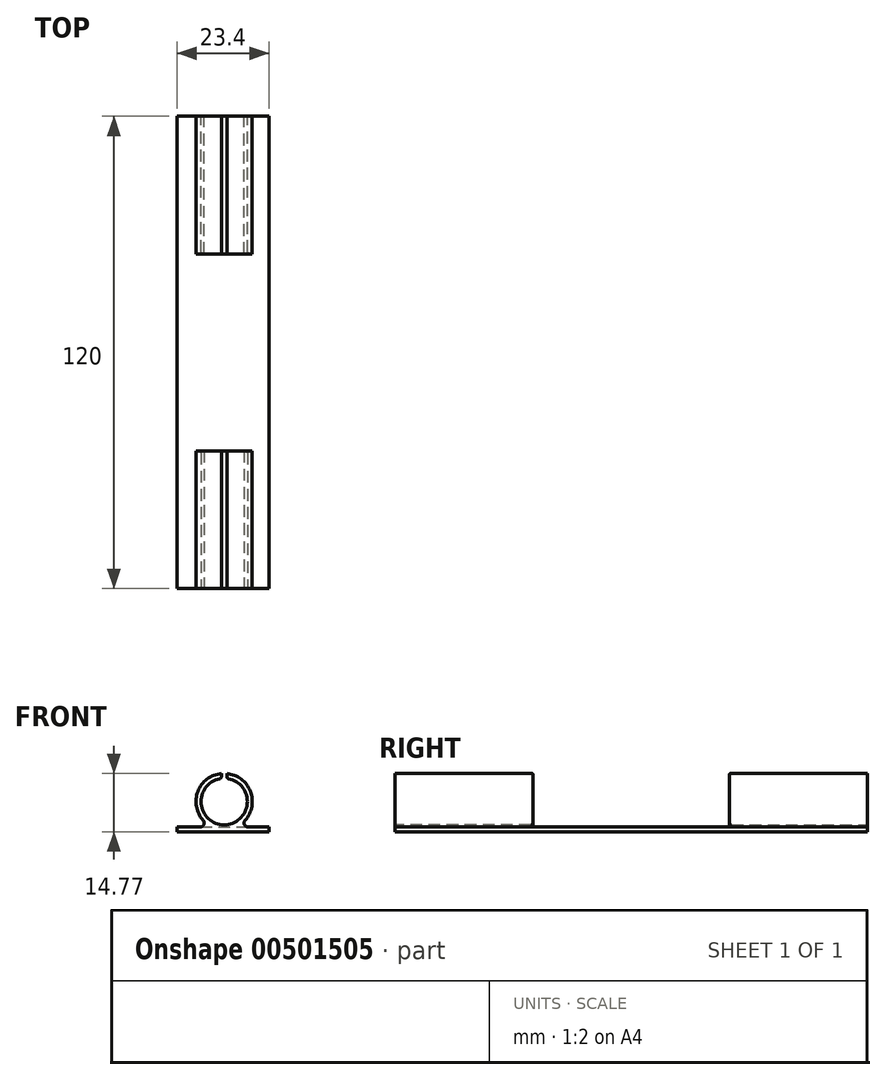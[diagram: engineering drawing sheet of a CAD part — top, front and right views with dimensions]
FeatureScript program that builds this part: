
annotation { "Feature Type Name" : "Feature", "Feature Type Description" : "" }
export const myFeature = defineFeature(function(context is Context, id is Id, definition is map)
    precondition{}
    {
        {
            var Q0;
            Q0=qCreatedBy(makeId("Top.planeOp"),FACE);
            var sketch = newSketch(context, id + "F0", { "sketchPlane" : qUnion([Q0])});
            skLineSegment(sketch, "E0.bottom", {"start": v(0, 0) * mm, "end": v(23.4, 0) * mm});
            skLineSegment(sketch, "E0.top", {"start": v(0, -60) * mm, "end": v(23.4, -60) * mm});
            skLineSegment(sketch, "E0.left", {"start": v(0, 0) * mm, "end": v(0, -60) * mm});
            skLineSegment(sketch, "E0.right", {"start": v(23.4, 0) * mm, "end": v(23.4, -60) * mm});
            skSolve(sketch);
        }
        {
            var Q0;
            Q0=makeQuery(id+"F0.imprint","IMPRINT",FACE,{"disambiguationData":[TD([[makeQuery(id+"F0.imprint","IMPRINT",EDGE,{"derivedFrom":sQuery(id+"F0.wireOp",EDGE,"E0.bottom")}),-1.0]])]});
            extrude(context, id + "F1", {"entities" : qUnion([Q0]), "depth" : 1.2 * mm});
        }
        {
            var Q0;
            Q0=qCreatedBy(makeId("Front.planeOp"),FACE);
            var sketch = newSketch(context, id + "F2", { "sketchPlane" : qUnion([Q0])});
            skCircle(sketch, "E1", {"center": v(12, 7.65) * mm, "radius": 5.9 * mm});
            skCircle(sketch, "E2", {"center": v(12, 7.65) * mm, "radius": 7.15 * mm});
            skLineSegment(sketch, "E3", {"start": v(0, 0.88) * mm, "end": v(0, 11.03) * mm, "construction": true});
            skLineSegment(sketch, "E4.bottom", {"start": v(12, 7.65) * mm, "end": v(12, 7.65) * mm});
            skLineSegment(sketch, "E5.bottom", {"start": v(12, 15.33) * mm, "end": v(11.3, 15.33) * mm});
            skLineSegment(sketch, "E5.top", {"start": v(12, 12.93) * mm, "end": v(11.3, 12.93) * mm});
            skLineSegment(sketch, "E5.left", {"start": v(12, 15.33) * mm, "end": v(12, 12.93) * mm});
            skLineSegment(sketch, "E5.right", {"start": v(11.3, 15.33) * mm, "end": v(11.3, 12.93) * mm});
            skLineSegment(sketch, "E6.MirrorCS", {"start": v(12, 15.33) * mm, "end": v(12.7, 15.33) * mm});
            skLineSegment(sketch, "E7.MirrorCS", {"start": v(12.7, 15.33) * mm, "end": v(12.7, 12.93) * mm});
            skLineSegment(sketch, "E8.MirrorCS", {"start": v(12, 12.93) * mm, "end": v(12.7, 12.93) * mm});
            skSolve(sketch);
        }
        {
            var Q0;
            {var subQ0=sQuery(id+"F2.wireOp",EDGE,"E7.MirrorCS");var subQ1=sQuery(id+"F2.wireOp",EDGE,"E1");var subQ2=makeQuery(id+"F2.imprint","INTERSECT",VERTEX,{"derivedFrom":[subQ1,subQ0]});Q0=makeQuery(id+"F2.imprint","IMPRINT",FACE,{"disambiguationData":[TD([[makeQuery(id+"F2.imprint","IMPRINT",EDGE,{"disambiguationData":[TD([[subQ2,1.0]])],"derivedFrom":subQ1}),-1.0]])]});}
            extrude(context, id + "F3", {"entities" : qUnion([Q0]), "operationType" : NewBodyOperationType.ADD, "depth" : 35 * mm});
        }
        {
            var Q0;
            Q0=makeQuery(id+"F3.boolean.opBoolean","INTERSECT",EDGE,{"disambiguationData":[OD(1.0)],"derivedFrom":[makeQuery(id+"F1.opExtrude","CAP_FACE",FACE,{"disambiguationData":[OSD([sQuery(id+"F0.wireOp",EDGE,"E0.bottom"),sQuery(id+"F0.wireOp",EDGE,"E0.top"),sQuery(id+"F0.wireOp",EDGE,"E0.left"),sQuery(id+"F0.wireOp",EDGE,"E0.right")])],"isStart":false}),makeQuery(id+"F3.opExtrude","SWEPT_FACE",FACE,{"disambiguationData":[OSD([sQuery(id+"F2.wireOp",EDGE,"E2")])]})]});
            fillet(context, id + "F4", {"entities" : qUnion([Q0]), "radius" : 1 * mm, "tangentPropagation" : true, "allowEdgeOverflow" : false});
        }
        {
            var Q0;
            Q0=makeQuery(id+"F3.boolean.opBoolean","INTERSECT",EDGE,{"disambiguationData":[OD(0.0)],"derivedFrom":[makeQuery(id+"F1.opExtrude","CAP_FACE",FACE,{"disambiguationData":[OSD([sQuery(id+"F0.wireOp",EDGE,"E0.bottom"),sQuery(id+"F0.wireOp",EDGE,"E0.top"),sQuery(id+"F0.wireOp",EDGE,"E0.left"),sQuery(id+"F0.wireOp",EDGE,"E0.right")])],"isStart":false}),makeQuery(id+"F3.opExtrude","SWEPT_FACE",FACE,{"disambiguationData":[OSD([sQuery(id+"F2.wireOp",EDGE,"E2")])]})]});
            fillet(context, id + "F5", {"entities" : qUnion([Q0]), "radius" : 1 * mm, "tangentPropagation" : true, "allowEdgeOverflow" : false});
        }
        {
            var Q0;
            Q0=makeQuery(id+"F3.opExtrude","CAP_EDGE",EDGE,{"disambiguationData":[OSD([sQuery(id+"F2.wireOp",EDGE,"E1")])],"isStart":false});
            fillet(context, id + "F6", {"entities" : qUnion([Q0]), "radius" : 0.5 * mm, "tangentPropagation" : true, "allowEdgeOverflow" : false});
        }
        {
            var Q0;
            Q0=makeQuery(id+"F3.opExtrude","SWEPT_EDGE",EDGE,{"disambiguationData":[OSD([sQuery(id+"F2.wireOp",EDGE,"E1"),sQuery(id+"F2.wireOp",EDGE,"E7.MirrorCS")])]});
            var Q1;
            Q1=makeQuery(id+"F3.opExtrude","SWEPT_EDGE",EDGE,{"disambiguationData":[OSD([sQuery(id+"F2.wireOp",EDGE,"E1"),sQuery(id+"F2.wireOp",EDGE,"E5.right")])]});
            fillet(context, id + "F7", {"entities" : qUnion([Q0, Q1]), "radius" : 0.5 * mm, "tangentPropagation" : true, "allowEdgeOverflow" : false});
        }
        {
            var Q0;
            Q0=makeQuery(id+"F1.opExtrude","SWEPT_BODY",BODY,{"disambiguationData":[OSD([sQuery(id+"F0.wireOp",EDGE,"E0.bottom"),sQuery(id+"F0.wireOp",EDGE,"E0.top"),sQuery(id+"F0.wireOp",EDGE,"E0.left"),sQuery(id+"F0.wireOp",EDGE,"E0.right")])]});
            var Q1;
            Q1=makeQuery(id+"F1.opExtrude","SWEPT_FACE",FACE,{"disambiguationData":[OSD([sQuery(id+"F0.wireOp",EDGE,"E0.top")])]});
            mirror(context, id + "F8", {"operationType" : NewBodyOperationType.ADD, "entities" : qUnion([Q0]), "mirrorPlane" : qUnion([Q1])});
        }
    });
